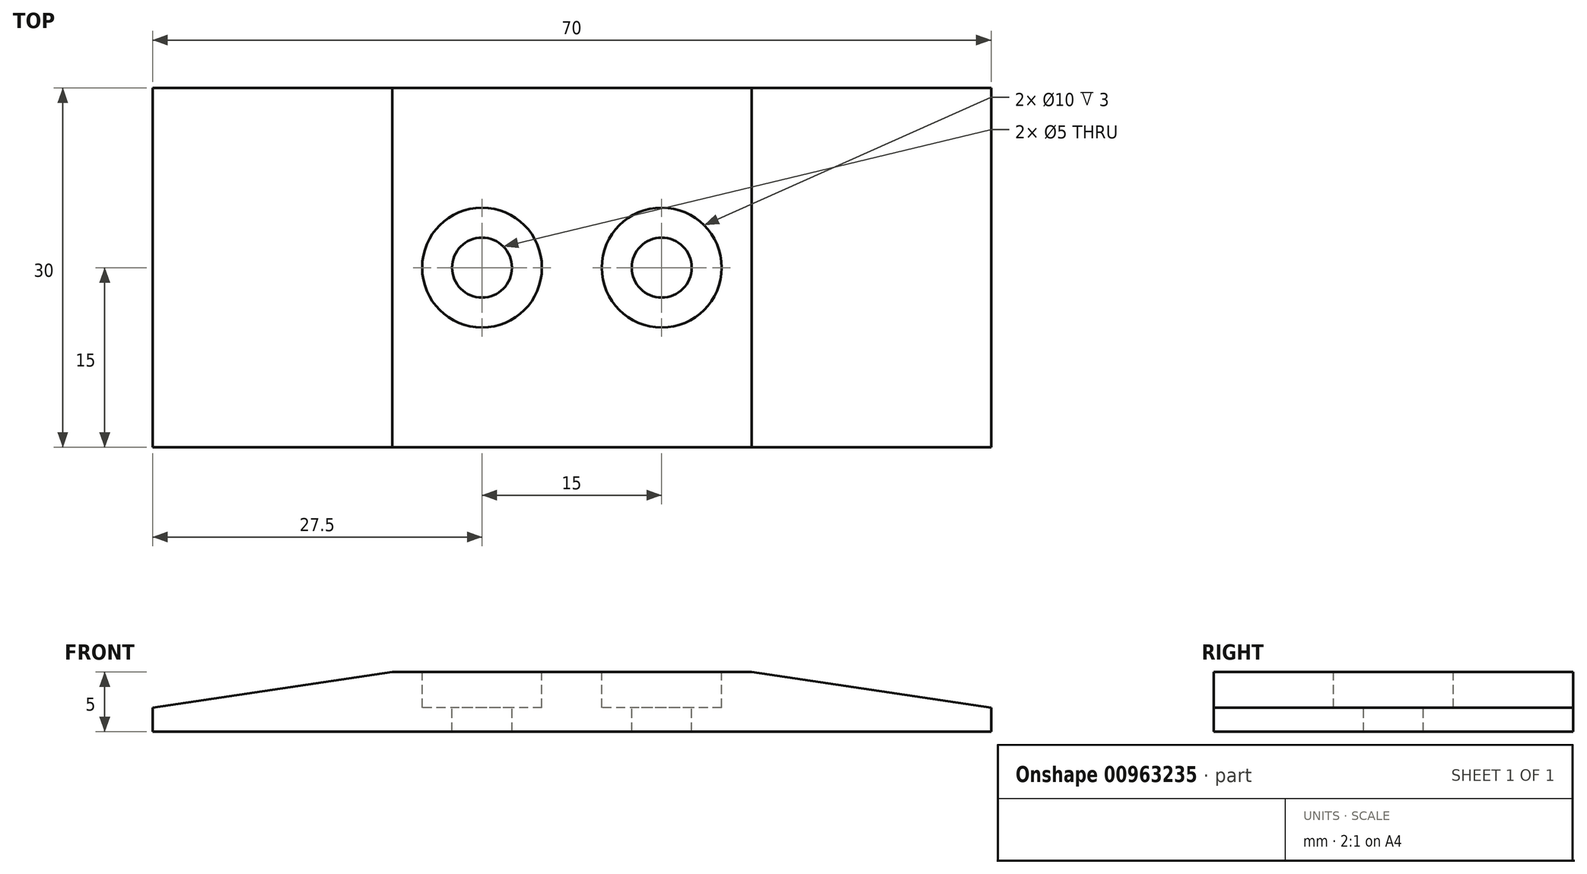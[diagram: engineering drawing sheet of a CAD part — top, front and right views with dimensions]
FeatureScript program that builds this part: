
annotation { "Feature Type Name" : "Feature", "Feature Type Description" : "" }
export const myFeature = defineFeature(function(context is Context, id is Id, definition is map)
    precondition{}
    {
        {
            var Q0;
            Q0=qCreatedBy(makeId("Front.planeOp"),FACE);
            var sketch = newSketch(context, id + "F0", { "sketchPlane" : qUnion([Q0])});
            skLineSegment(sketch, "E0", {"start": v(0, 0) * mm, "end": v(-35, 0) * mm});
            skLineSegment(sketch, "E1", {"start": v(-35, 0) * mm, "end": v(-35, 2) * mm});
            skLineSegment(sketch, "E2", {"start": v(0, 0) * mm, "end": v(35, 0) * mm});
            skLineSegment(sketch, "E3", {"start": v(35, 0) * mm, "end": v(35, 2) * mm});
            skLineSegment(sketch, "E4", {"start": v(0, 0) * mm, "end": v(0, 5) * mm, "construction": true});
            skLineSegment(sketch, "E5", {"start": v(0, 5) * mm, "end": v(-15, 5) * mm});
            skLineSegment(sketch, "E6", {"start": v(-15, 5) * mm, "end": v(-35, 2) * mm});
            skLineSegment(sketch, "E7", {"start": v(0, 5) * mm, "end": v(15, 5) * mm});
            skLineSegment(sketch, "E8", {"start": v(15, 5) * mm, "end": v(35, 2) * mm});
            skSolve(sketch);
        }
        {
            var Q0;
            Q0 = qSketchRegion(id + "F0", true);
            extrude(context, id + "F1", {"entities" : qUnion([Q0]), "depth" : 30 * mm, "offsetDistance" : 25 * mm});
        }
        {
            var Q0;
            Q0=makeQuery(id+"F1.opExtrude","SWEPT_FACE",FACE,{"disambiguationData":[OSD([sQuery(id+"F0.wireOp",EDGE,"E5"),sQuery(id+"F0.wireOp",EDGE,"E7")])]});
            var sketch = newSketch(context, id + "F2", { "sketchPlane" : qUnion([Q0])});
            skLineSegment(sketch, "E9", {"start": v(-15, -15) * mm, "end": v(15, -15) * mm, "construction": true});
            skLineSegment(sketch, "E10", {"start": v(0, -15) * mm, "end": v(-7.5, -15) * mm});
            skLineSegment(sketch, "E11", {"start": v(0, -15) * mm, "end": v(7.5, -15) * mm, "construction": true});
            skCircle(sketch, "E12", {"center": v(-7.5, -15) * mm, "radius": 5 * mm});
            skCircle(sketch, "E13", {"center": v(7.5, -15) * mm, "radius": 5 * mm});
            skSolve(sketch);
        }
        {
            var Q0;
            Q0 = qSketchRegion(id + "F2", true);
            extrude(context, id + "F3", {"entities" : qUnion([Q0]), "operationType" : NewBodyOperationType.REMOVE, "oppositeDirection" : true, "depth" : 3 * mm, "offsetDistance" : 25 * mm});
        }
        {
            var Q0;
            Q0=makeQuery(id+"F3.boolean.opBoolean","COPY",FACE,{"derivedFrom":makeQuery(id+"F3.opExtrude","CAP_FACE",FACE,{"disambiguationData":[OSD([sQuery(id+"F2.wireOp",EDGE,"E12")])],"isStart":false})});
            var sketch = newSketch(context, id + "F4", { "sketchPlane" : qUnion([Q0])});
            skCircle(sketch, "E14", {"center": v(-7.5, -15) * mm, "radius": 2.5 * mm});
            skSolve(sketch);
        }
        {
            var Q0;
            Q0 = qSketchRegion(id + "F4", true);
            extrude(context, id + "F5", {"entities" : qUnion([Q0]), "operationType" : NewBodyOperationType.REMOVE, "oppositeDirection" : true, "depth" : 10 * mm, "offsetDistance" : 25 * mm});
        }
        {
            var Q0;
            Q0=makeQuery(id+"F3.boolean.opBoolean","COPY",FACE,{"derivedFrom":makeQuery(id+"F3.opExtrude","CAP_FACE",FACE,{"disambiguationData":[OSD([sQuery(id+"F2.wireOp",EDGE,"E13")])],"isStart":false})});
            var sketch = newSketch(context, id + "F6", { "sketchPlane" : qUnion([Q0])});
            skCircle(sketch, "E15", {"center": v(7.5, -15) * mm, "radius": 2.5 * mm});
            skSolve(sketch);
        }
        {
            var Q0;
            Q0 = qSketchRegion(id + "F6", true);
            extrude(context, id + "F7", {"entities" : qUnion([Q0]), "operationType" : NewBodyOperationType.REMOVE, "oppositeDirection" : true, "depth" : 25 * mm, "offsetDistance" : 25 * mm});
        }
    });
